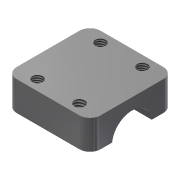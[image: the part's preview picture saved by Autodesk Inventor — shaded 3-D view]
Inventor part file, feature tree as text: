
AUTODESK INVENTOR PART (.ipt)
format: ipt  version: 2015 (Build 190159000, 159)  size: 138,240 bytes
history: native  units: mm
features: hole x5, extrude x1, fillet x1, sketch x1
ambient origin geometry x8: Origin, YZ Plane, XZ Plane, XY Plane, X Axis, Y Axis, Z Axis, Center Point
bodies: Body1 (feature_tree)
feature tree (8):
  extrude  "Extrusion2"  Depth=40.0mm
  hole  "Hole3"  [1 undecoded]
  hole  "Hole4"  [1 undecoded]
  hole  "Hole5"  [1 undecoded]
  hole  "Hole6"  [1 undecoded]
  hole  "Hole7"  [1 undecoded]
  fillet  "Fillet1"  [1 undecoded]
  sketch  "Sketch4"  dims[d37=40.0mm d38=40.0mm d39=14.0mm d40=0.0mm d50=5.0mm d51=10.0mm d52=4.917mm d53=12.0mm d54=9.0mm d55=8.0mm d56=90.0deg d57=17.1mm d58=20.594885mm d59=5.0mm d60=10.0mm d61=4.917mm d62=12.0mm d63=9.0mm d64=8.0mm d65=90.0deg d66=17.1mm d67=20.594885mm d68=10.0mm d69=5.0mm d70=4.978mm d71=12.7mm d72=9.0mm d73=8.0mm d74=90.0deg d75=19.05mm d76=20.594885mm d77=10.0mm d78=5.0mm d79=4.917mm d80=12.0mm d81=9.0mm d82=8.0mm d83=90.0deg d84=17.1mm d85=20.594885mm d86=15.0mm d87=20.0mm d88=19.0mm d89=6.0mm d90=4.0mm d91=2.0mm d92=90.0deg d93=8.0mm d94=20.594885mm d95=5.0mm]
note: 6 required parameter values undecoded (feature->parameter linkage not recoverable at this tier; creation-order binding heuristic only, values carry confidence <= 0.55)
